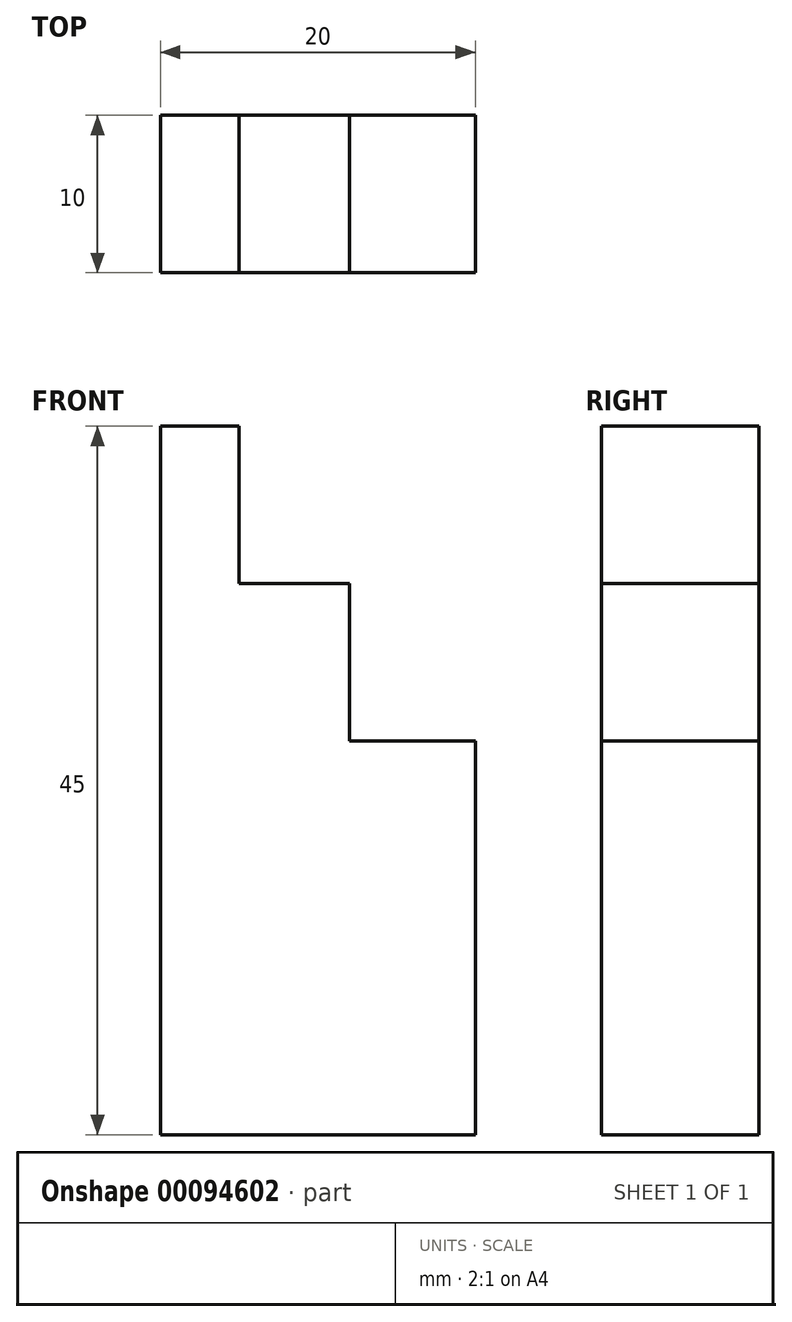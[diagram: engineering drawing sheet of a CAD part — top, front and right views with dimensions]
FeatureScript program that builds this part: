
annotation { "Feature Type Name" : "Feature", "Feature Type Description" : "" }
export const myFeature = defineFeature(function(context is Context, id is Id, definition is map)
    precondition{}
    {
        {
            var Q0;
            Q0=qCreatedBy(makeId("Front.planeOp"),FACE);
            var sketch = newSketch(context, id + "F0", { "sketchPlane" : qUnion([Q0])});
            skLineSegment(sketch, "E0", {"start": v(0, 0) * mm, "end": v(0, 45) * mm});
            skLineSegment(sketch, "E1", {"start": v(0, 45) * mm, "end": v(5, 45) * mm});
            skLineSegment(sketch, "E2", {"start": v(5, 45) * mm, "end": v(5, 35) * mm});
            skLineSegment(sketch, "E3", {"start": v(5, 35) * mm, "end": v(12, 35) * mm});
            skLineSegment(sketch, "E4", {"start": v(12, 35) * mm, "end": v(12, 25) * mm});
            skLineSegment(sketch, "E5", {"start": v(12, 25) * mm, "end": v(20, 25) * mm});
            skLineSegment(sketch, "E6", {"start": v(20, 25) * mm, "end": v(20, 0) * mm});
            skLineSegment(sketch, "E7", {"start": v(20, 0) * mm, "end": v(0, 0) * mm});
            skSolve(sketch);
        }
        {
            var Q0;
            Q0 = qSketchRegion(id + "F0", true);
            extrude(context, id + "F1", {"entities" : qUnion([Q0]), "depth" : 10 * mm});
        }
    });
